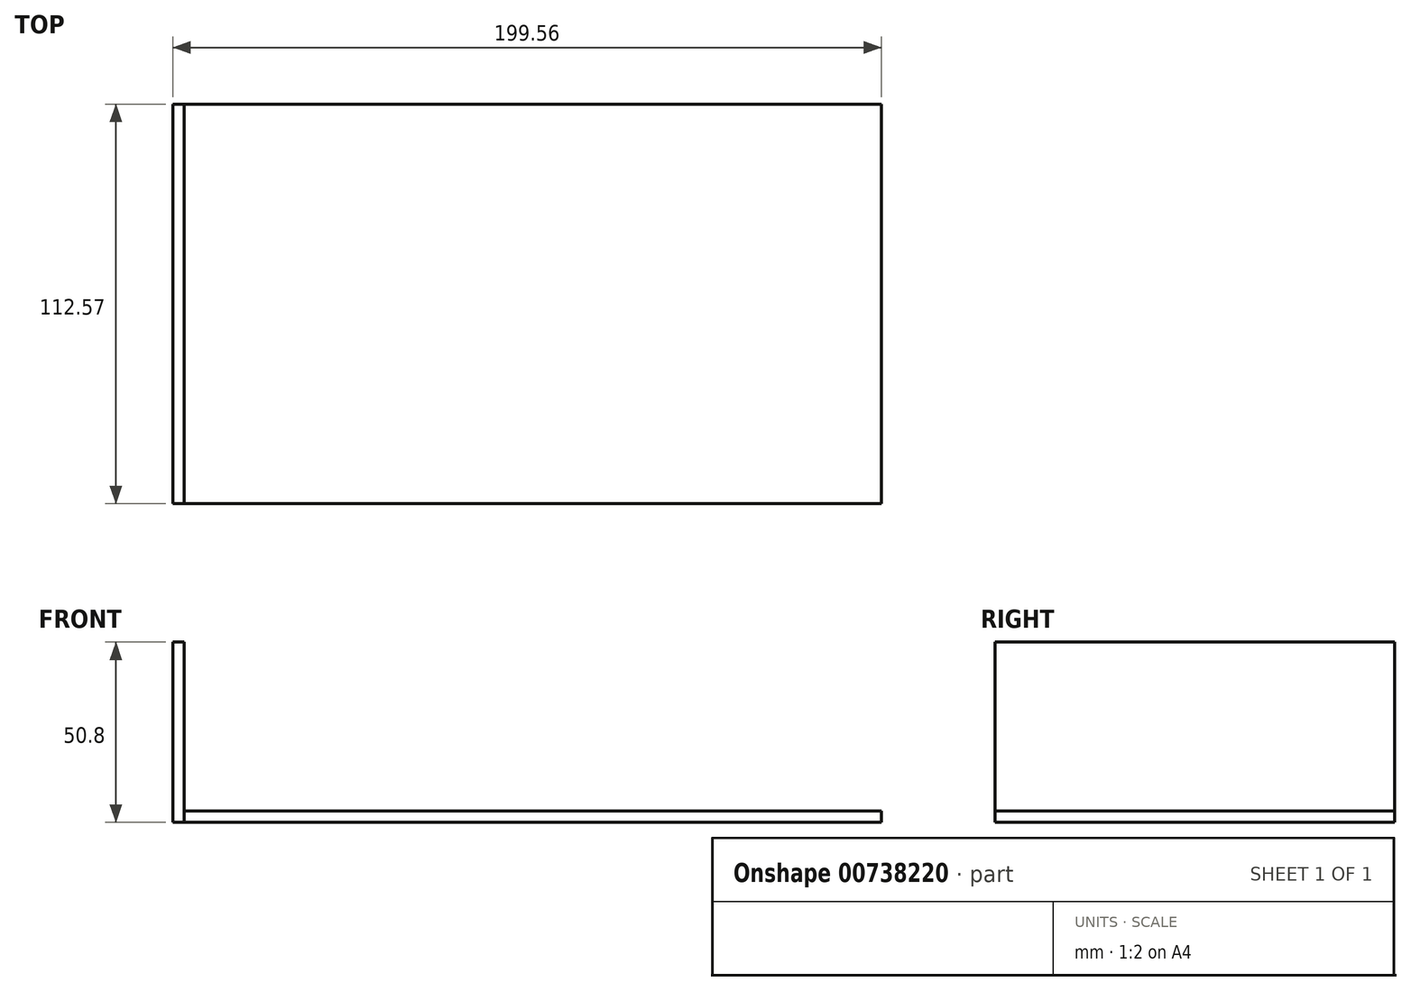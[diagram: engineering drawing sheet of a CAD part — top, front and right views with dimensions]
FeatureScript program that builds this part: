
annotation { "Feature Type Name" : "Feature", "Feature Type Description" : "" }
export const myFeature = defineFeature(function(context is Context, id is Id, definition is map)
    precondition{}
    {
        {
            var Q0;
            Q0=qCreatedBy(makeId("Top.planeOp"),FACE);
            var sketch = newSketch(context, id + "F0", { "sketchPlane" : qUnion([Q0])});
            skLineSegment(sketch, "E0.top", {"start": v(-96.49, -56.17) * mm, "end": v(99.9, -56.17) * mm});
            skLineSegment(sketch, "E0.right", {"start": v(99.9, 56.4) * mm, "end": v(99.9, -56.17) * mm});
            skLineSegment(sketch, "E1", {"start": v(-96.49, 56.4) * mm, "end": v(-96.49, -56.17) * mm});
            skLineSegment(sketch, "E2", {"start": v(-96.49, 56.4) * mm, "end": v(99.9, 56.4) * mm});
            skSolve(sketch);
        }
        {
            var Q0;
            Q0=makeQuery(id+"F0.imprint","IMPRINT",FACE,{"disambiguationData":[TD([[makeQuery(id+"F0.imprint","IMPRINT",EDGE,{"derivedFrom":sQuery(id+"F0.wireOp",EDGE,"E0.top")}),1.0]])]});
            extrude(context, id + "F1", {"entities" : qUnion([Q0]), "depth" : 3.17 * mm, "offsetDistance" : 25.4 * mm});
        }
        {
            var Q0;
            Q0=qCreatedBy(makeId("Top.planeOp"),FACE);
            var sketch = newSketch(context, id + "F2", { "sketchPlane" : qUnion([Q0])});
            skLineSegment(sketch, "E3.bottom", {"start": v(-99.66, 56.4) * mm, "end": v(-96.49, 56.4) * mm});
            skLineSegment(sketch, "E3.top", {"start": v(-99.66, -56.17) * mm, "end": v(-96.49, -56.17) * mm});
            skLineSegment(sketch, "E3.left", {"start": v(-99.66, 56.4) * mm, "end": v(-99.66, -56.17) * mm});
            skLineSegment(sketch, "E3.right", {"start": v(-96.49, 56.4) * mm, "end": v(-96.49, -56.17) * mm});
            skSolve(sketch);
        }
        {
            var Q0;
            Q0 = qSketchRegion(id + "F2", true);
            extrude(context, id + "F3", {"entities" : qUnion([Q0]), "depth" : 50.8 * mm, "offsetDistance" : 25.4 * mm});
        }
    });
